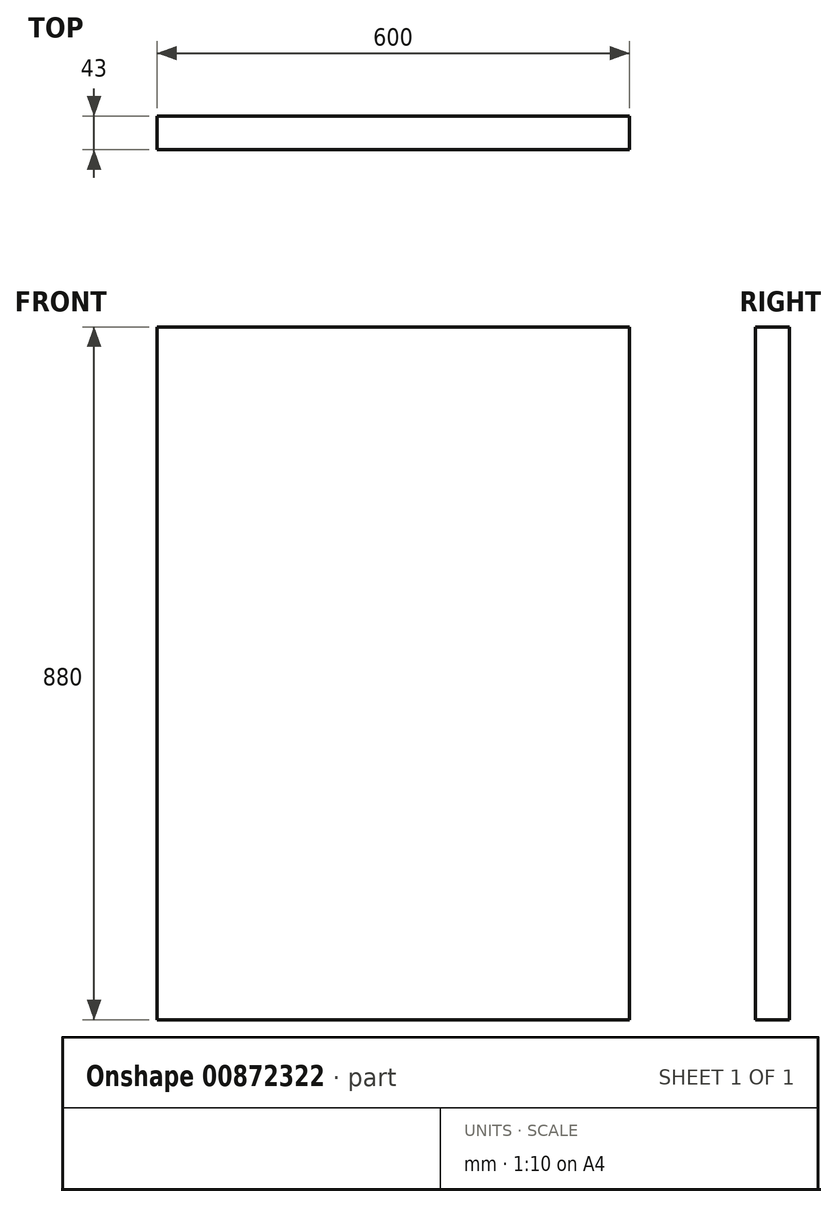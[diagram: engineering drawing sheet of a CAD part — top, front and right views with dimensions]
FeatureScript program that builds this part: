
annotation { "Feature Type Name" : "Feature", "Feature Type Description" : "" }
export const myFeature = defineFeature(function(context is Context, id is Id, definition is map)
    precondition{}
    {
        {
            var Q0;
            Q0=qCreatedBy(makeId("Front.planeOp"),FACE);
            var sketch = newSketch(context, id + "F0", { "sketchPlane" : qUnion([Q0])});
            skLineSegment(sketch, "E0", {"start": v(0, 0) * mm, "end": v(0, 880) * mm});
            skLineSegment(sketch, "E1", {"start": v(0, 880) * mm, "end": v(600, 880) * mm});
            skLineSegment(sketch, "E2", {"start": v(600, 880) * mm, "end": v(600, 0) * mm});
            skLineSegment(sketch, "E3", {"start": v(600, 0) * mm, "end": v(0, 0) * mm});
            skSolve(sketch);
        }
        {
            var Q0;
            Q0=makeQuery(id+"F0.imprint","IMPRINT",FACE,{"disambiguationData":[TD([[makeQuery(id+"F0.imprint","IMPRINT",EDGE,{"derivedFrom":sQuery(id+"F0.wireOp",EDGE,"E0")}),-1.0]])]});
            extrude(context, id + "F1", {"entities" : qUnion([Q0]), "depth" : 25 * mm, "offsetDistance" : 25 * mm});
        }
        {
            var Q0;
            Q0=makeQuery(id+"F1.opExtrude","CAP_FACE",FACE,{"disambiguationData":[OSD([sQuery(id+"F0.wireOp",EDGE,"E0"),sQuery(id+"F0.wireOp",EDGE,"E1"),sQuery(id+"F0.wireOp",EDGE,"E2"),sQuery(id+"F0.wireOp",EDGE,"E3")])],"isStart":false});
            extrude(context, id + "F2", {"entities" : qUnion([Q0]), "operationType" : NewBodyOperationType.ADD, "depth" : 18 * mm, "offsetDistance" : 25 * mm});
        }
    });
